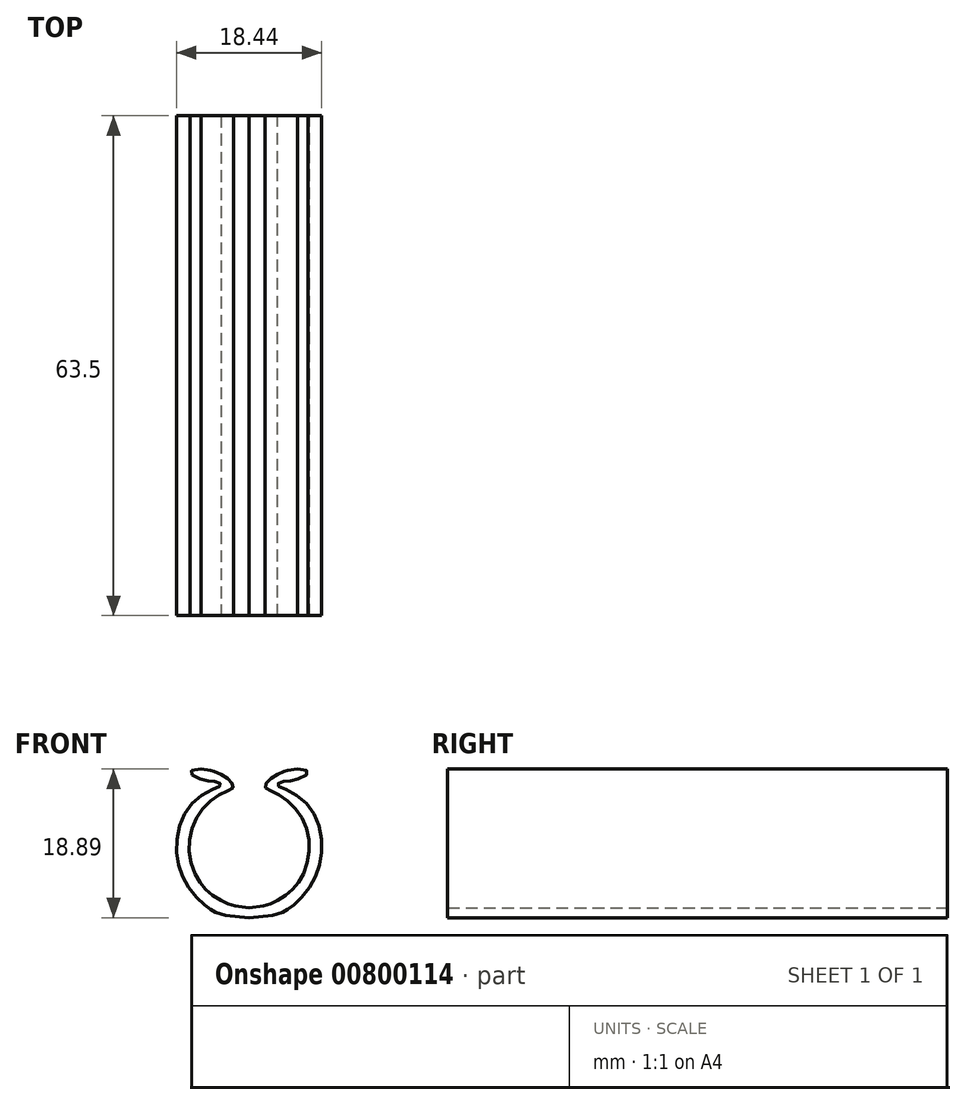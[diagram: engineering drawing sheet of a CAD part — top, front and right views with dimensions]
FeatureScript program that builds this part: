
annotation { "Feature Type Name" : "Feature", "Feature Type Description" : "" }
export const myFeature = defineFeature(function(context is Context, id is Id, definition is map)
    precondition{}
    {
        {
            var Q0;
            Q0=qCreatedBy(makeId("Front.planeOp"),FACE);
            var sketch = newSketch(context, id + "F0", { "sketchPlane" : qUnion([Q0])});
            skFitSpline(sketch, "E0", {"points": [v(-6.13, 9.94) * mm, v(-4.69, 9.75) * mm, v(-3.56, 9.25) * mm, v(-2.32, 8.37) * mm, v(-2.03, 7.65) * mm, v(-2.92, 7.1) * mm, v(-5.3, 5.55) * mm, v(-7.2, 2.7) * mm, v(-7.57, -1.03) * mm, v(-6.42, -4.23) * mm, v(-4.87, -5.92) * mm, v(-2.92, -7.1) * mm, v(0, -7.67) * mm], "startDerivative": vector(58.36, -7.3) * mm, "endDerivative": vector(59.97, -5.94) * mm});
            skLineSegment(sketch, "E1", {"start": v(0, -7.67) * mm, "end": v(0, -8.94) * mm});
            skFitSpline(sketch, "E2", {"points": [v(0, -8.94) * mm, v(-4.67, -8) * mm, v(-5.72, -7.26) * mm, v(-7.94, -4.67) * mm, v(-9.14, -1.26) * mm, v(-8.78, 2.93) * mm, v(-6.6, 6.2) * mm, v(-3.96, 7.66) * mm, v(-3.58, 7.9) * mm, v(-3.93, 8.3) * mm, v(-4.89, 8.42) * mm, v(-6.3, 8.7) * mm, v(-7.5, 9.53) * mm, v(-6.13, 9.94) * mm], "startDerivative": vector(-98.3, 5.65) * mm, "endDerivative": vector(32.12, -1.56) * mm});
            skFitSpline(sketch, "E3.MirrorCS", {"points": [v(6.13, 9.94) * mm, v(4.69, 9.75) * mm, v(3.56, 9.25) * mm, v(2.32, 8.37) * mm, v(2.03, 7.65) * mm, v(2.92, 7.1) * mm, v(5.3, 5.55) * mm, v(7.2, 2.7) * mm, v(7.57, -1.03) * mm, v(6.42, -4.23) * mm, v(4.87, -5.92) * mm, v(2.92, -7.1) * mm, v(0, -7.67) * mm], "startDerivative": vector(-58.36, -7.3) * mm, "endDerivative": vector(-59.97, -5.94) * mm});
            skFitSpline(sketch, "E4.MirrorCS", {"points": [v(0, -8.94) * mm, v(4.67, -8) * mm, v(5.72, -7.26) * mm, v(7.94, -4.67) * mm, v(9.14, -1.26) * mm, v(8.78, 2.93) * mm, v(6.6, 6.2) * mm, v(3.96, 7.66) * mm, v(3.58, 7.9) * mm, v(3.93, 8.3) * mm, v(4.89, 8.42) * mm, v(6.3, 8.7) * mm, v(7.5, 9.53) * mm, v(6.13, 9.94) * mm], "startDerivative": vector(98.3, 5.65) * mm, "endDerivative": vector(-32.12, -1.56) * mm});
            skSolve(sketch);
        }
        {
            var Q0;
            Q0 = qSketchRegion(id + "F0", true);
            extrude(context, id + "F1", {"entities" : qUnion([Q0]), "depth" : 63.5 * mm, "offsetDistance" : 25.4 * mm});
        }
    });
